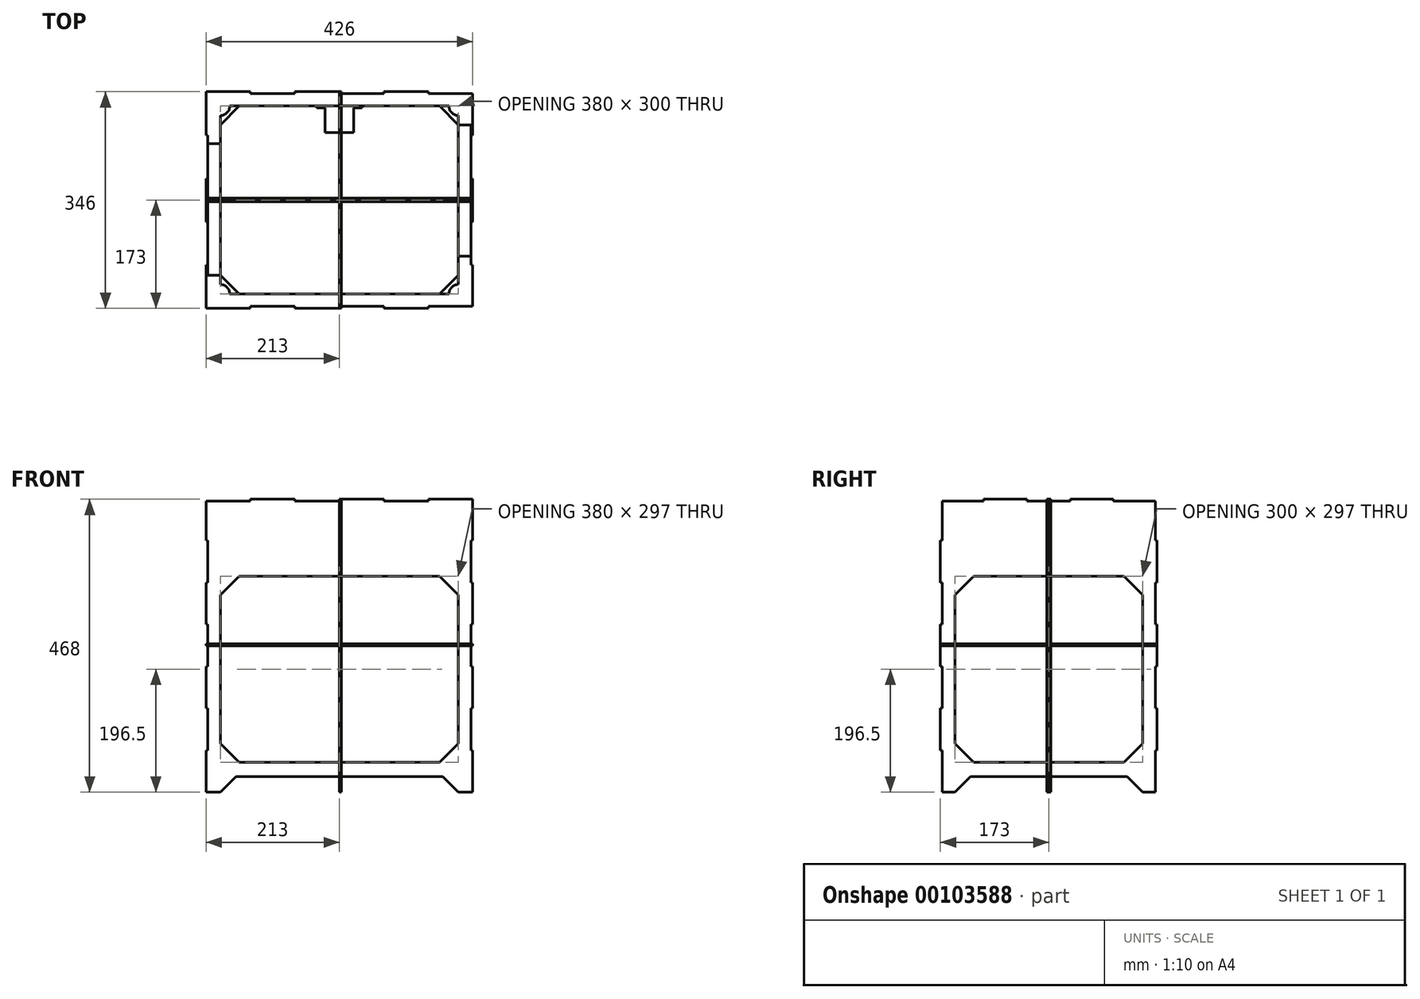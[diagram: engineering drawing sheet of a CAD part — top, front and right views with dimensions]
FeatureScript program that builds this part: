
annotation { "Feature Type Name" : "Feature", "Feature Type Description" : "" }
export const myFeature = defineFeature(function(context is Context, id is Id, definition is map)
    precondition{}
    {
        {
            assignVariable(context, id + "F0", {"name" : "thick", "anyValue" : 3});
        }
        {
            var Q0;
            Q0=qCreatedBy(makeId("Top.planeOp"),FACE);
            var sketch = newSketch(context, id + "F1", { "sketchPlane" : qUnion([Q0])});
            skLineSegment(sketch, "E0.bottom", {"start": v(213, -173) * mm, "end": v(-213, -173) * mm});
            skLineSegment(sketch, "E0.top", {"start": v(213, 173) * mm, "end": v(-213, 173) * mm});
            skLineSegment(sketch, "E0.left", {"start": v(213, -173) * mm, "end": v(213, 173) * mm});
            skLineSegment(sketch, "E0.right", {"start": v(-213, -173) * mm, "end": v(-213, 173) * mm});
            skPoint(sketch, "E0.middle", {"position": v(0, 0) * mm});
            skLineSegment(sketch, "E1.bottom", {"start": v(190, -150) * mm, "end": v(-190, -150) * mm, "construction": true});
            skLineSegment(sketch, "E1.top", {"start": v(190, 150) * mm, "end": v(-190, 150) * mm, "construction": true});
            skLineSegment(sketch, "E1.left", {"start": v(190, -150) * mm, "end": v(190, 150) * mm, "construction": true});
            skLineSegment(sketch, "E1.right", {"start": v(-190, -150) * mm, "end": v(-190, 150) * mm, "construction": true});
            skLineSegment(sketch, "E2", {"start": v(-160, 150) * mm, "end": v(-190, 120) * mm});
            skLineSegment(sketch, "E3", {"start": v(-190, 120) * mm, "end": v(-190, -120) * mm});
            skLineSegment(sketch, "E4", {"start": v(-190, -120) * mm, "end": v(-160, -150) * mm});
            skLineSegment(sketch, "E5", {"start": v(-160, -150) * mm, "end": v(160, -150) * mm});
            skLineSegment(sketch, "E6", {"start": v(160, -150) * mm, "end": v(190, -120) * mm});
            skLineSegment(sketch, "E7", {"start": v(190, -120) * mm, "end": v(190, 120) * mm});
            skLineSegment(sketch, "E8", {"start": v(190, 120) * mm, "end": v(160, 150) * mm});
            skLineSegment(sketch, "E9", {"start": v(160, 150) * mm, "end": v(-160, 150) * mm});
            skLineSegment(sketch, "E10.bottom", {"start": v(-142, 173) * mm, "end": v(-71, 173) * mm});
            skLineSegment(sketch, "E10.top", {"start": v(-142, 170) * mm, "end": v(-71, 170) * mm});
            skLineSegment(sketch, "E10.left", {"start": v(-142, 173) * mm, "end": v(-142, 170) * mm});
            skLineSegment(sketch, "E10.right", {"start": v(-71, 173) * mm, "end": v(-71, 170) * mm});
            skLineSegment(sketch, "E11.bottom", {"start": v(0, 173) * mm, "end": v(71, 173) * mm});
            skLineSegment(sketch, "E11.top", {"start": v(0, 170) * mm, "end": v(71, 170) * mm});
            skLineSegment(sketch, "E11.left", {"start": v(0, 173) * mm, "end": v(0, 170) * mm});
            skLineSegment(sketch, "E11.right", {"start": v(71, 173) * mm, "end": v(71, 170) * mm});
            skLineSegment(sketch, "E12.bottom", {"start": v(142, 173) * mm, "end": v(213, 173) * mm});
            skLineSegment(sketch, "E12.top", {"start": v(142, 170) * mm, "end": v(213, 170) * mm});
            skLineSegment(sketch, "E12.left", {"start": v(142, 173) * mm, "end": v(142, 170) * mm});
            skLineSegment(sketch, "E12.right", {"start": v(213, 173) * mm, "end": v(213, 170) * mm});
            skLineSegment(sketch, "E13.bottom", {"start": v(-142, -173) * mm, "end": v(-71, -173) * mm});
            skLineSegment(sketch, "E13.top", {"start": v(-142, -170) * mm, "end": v(-71, -170) * mm});
            skLineSegment(sketch, "E13.left", {"start": v(-142, -173) * mm, "end": v(-142, -170) * mm});
            skLineSegment(sketch, "E13.right", {"start": v(-71, -173) * mm, "end": v(-71, -170) * mm});
            skLineSegment(sketch, "E14.bottom", {"start": v(0, -173) * mm, "end": v(71, -173) * mm});
            skLineSegment(sketch, "E14.top", {"start": v(0, -170) * mm, "end": v(71, -170) * mm});
            skLineSegment(sketch, "E14.left", {"start": v(0, -173) * mm, "end": v(0, -170) * mm});
            skLineSegment(sketch, "E14.right", {"start": v(71, -173) * mm, "end": v(71, -170) * mm});
            skLineSegment(sketch, "E15.bottom", {"start": v(142, -173) * mm, "end": v(213, -173) * mm});
            skLineSegment(sketch, "E15.top", {"start": v(142, -170) * mm, "end": v(213, -170) * mm});
            skLineSegment(sketch, "E15.left", {"start": v(142, -173) * mm, "end": v(142, -170) * mm});
            skLineSegment(sketch, "E15.right", {"start": v(213, -173) * mm, "end": v(213, -170) * mm});
            skLineSegment(sketch, "E16.bottom", {"start": v(-213, 103) * mm, "end": v(-210, 103) * mm});
            skLineSegment(sketch, "E16.top", {"start": v(-213, 34) * mm, "end": v(-210, 34) * mm});
            skLineSegment(sketch, "E16.left", {"start": v(-213, 103) * mm, "end": v(-213, 34) * mm});
            skLineSegment(sketch, "E16.right", {"start": v(-210, 103) * mm, "end": v(-210, 34) * mm});
            skLineSegment(sketch, "E17.0.1.0", {"start": v(-213, -35) * mm, "end": v(-210, -35) * mm});
            skLineSegment(sketch, "E17.0.1.1", {"start": v(-210, -35) * mm, "end": v(-210, -104) * mm});
            skLineSegment(sketch, "E17.0.1.2", {"start": v(-213, -104) * mm, "end": v(-210, -104) * mm});
            skLineSegment(sketch, "E17.direction1", {"start": v(-213, 103) * mm, "end": v(-210, 103) * mm, "construction": true});
            skLineSegment(sketch, "E17.direction2", {"start": v(-213, 103) * mm, "end": v(-213, -35) * mm, "construction": true});
            skLineSegment(sketch, "E18.bottom", {"start": v(213, 103) * mm, "end": v(210, 103) * mm});
            skLineSegment(sketch, "E18.top", {"start": v(213, 34) * mm, "end": v(210, 34) * mm});
            skLineSegment(sketch, "E18.left", {"start": v(213, 103) * mm, "end": v(213, 34) * mm});
            skLineSegment(sketch, "E18.right", {"start": v(210, 103) * mm, "end": v(210, 34) * mm});
            skLineSegment(sketch, "E19.bottom", {"start": v(213, -35) * mm, "end": v(210, -35) * mm});
            skLineSegment(sketch, "E19.top", {"start": v(213, -104) * mm, "end": v(210, -104) * mm});
            skLineSegment(sketch, "E19.left", {"start": v(213, -35) * mm, "end": v(213, -104) * mm});
            skLineSegment(sketch, "E19.right", {"start": v(210, -35) * mm, "end": v(210, -104) * mm});
            skSolve(sketch);
        }
        {
            var Q0;
            Q0=makeQuery(id+"F1.imprint","IMPRINT",FACE,{"disambiguationData":[TD([[makeQuery(id+"F1.imprint","IMPRINT",EDGE,{"derivedFrom":sQuery(id+"F1.wireOp",EDGE,"E0.left")}),1.0]])]});
            extrude(context, id + "F2", {"entities" : qUnion([Q0]), "depth" : (getVariable(context, 'thick')) * mm});
        }
        {
            var Q0;
            Q0=qCreatedBy(makeId("Front.planeOp"),FACE);
            var sketch = newSketch(context, id + "F3", { "sketchPlane" : qUnion([Q0])});
            skLineSegment(sketch, "E20.bottom", {"start": v(213, -234) * mm, "end": v(-213, -234) * mm});
            skLineSegment(sketch, "E20.top", {"start": v(213, 234) * mm, "end": v(-213, 234) * mm});
            skLineSegment(sketch, "E20.left", {"start": v(213, -234) * mm, "end": v(213, 234) * mm});
            skLineSegment(sketch, "E20.right", {"start": v(-213, -234) * mm, "end": v(-213, 234) * mm});
            skPoint(sketch, "E20.middle", {"position": v(0, 0) * mm});
            skLineSegment(sketch, "E21.bottom", {"start": v(-190, 111) * mm, "end": v(190, 111) * mm, "construction": true});
            skLineSegment(sketch, "E21.top", {"start": v(-190, -186) * mm, "end": v(190, -186) * mm, "construction": true});
            skLineSegment(sketch, "E21.left", {"start": v(-190, 111) * mm, "end": v(-190, -186) * mm, "construction": true});
            skLineSegment(sketch, "E21.right", {"start": v(190, 111) * mm, "end": v(190, -186) * mm, "construction": true});
            skLineSegment(sketch, "E22", {"start": v(-190, -234) * mm, "end": v(-165, -209) * mm});
            skLineSegment(sketch, "E23", {"start": v(-165, -209) * mm, "end": v(165, -209) * mm});
            skLineSegment(sketch, "E24", {"start": v(165, -209) * mm, "end": v(190, -234) * mm});
            skLineSegment(sketch, "E25", {"start": v(-160, 111) * mm, "end": v(-190, 81) * mm});
            skLineSegment(sketch, "E26", {"start": v(-190, 81) * mm, "end": v(-190, -156) * mm});
            skLineSegment(sketch, "E27", {"start": v(-190, -156) * mm, "end": v(-160, -186) * mm});
            skLineSegment(sketch, "E28", {"start": v(-160, -186) * mm, "end": v(160, -186) * mm});
            skLineSegment(sketch, "E29", {"start": v(160, -186) * mm, "end": v(190, -156) * mm});
            skLineSegment(sketch, "E30", {"start": v(190, -156) * mm, "end": v(190, 81) * mm});
            skLineSegment(sketch, "E31", {"start": v(190, 81) * mm, "end": v(160, 111) * mm});
            skLineSegment(sketch, "E32", {"start": v(160, 111) * mm, "end": v(-160, 111) * mm});
            skLineSegment(sketch, "E33.bottom", {"start": v(-213, 234) * mm, "end": v(-142, 234) * mm});
            skLineSegment(sketch, "E33.top", {"start": v(-213, 231) * mm, "end": v(-142, 231) * mm});
            skLineSegment(sketch, "E33.left", {"start": v(-213, 234) * mm, "end": v(-213, 231) * mm});
            skLineSegment(sketch, "E33.right", {"start": v(-142, 234) * mm, "end": v(-142, 231) * mm});
            skLineSegment(sketch, "E34.1.0.0", {"start": v(-71, 231) * mm, "end": v(0, 231) * mm});
            skLineSegment(sketch, "E34.1.0.1", {"start": v(-71, 234) * mm, "end": v(-71, 231) * mm});
            skLineSegment(sketch, "E34.1.0.2", {"start": v(0, 234) * mm, "end": v(0, 231) * mm});
            skLineSegment(sketch, "E34.2.0.0", {"start": v(71, 231) * mm, "end": v(142, 231) * mm});
            skLineSegment(sketch, "E34.2.0.1", {"start": v(71, 234) * mm, "end": v(71, 231) * mm});
            skLineSegment(sketch, "E34.2.0.2", {"start": v(142, 234) * mm, "end": v(142, 231) * mm});
            skLineSegment(sketch, "E34.direction1", {"start": v(-213, 231) * mm, "end": v(-71, 231) * mm, "construction": true});
            skLineSegment(sketch, "E35.bottom", {"start": v(-213, 168) * mm, "end": v(-210, 168) * mm});
            skLineSegment(sketch, "E35.top", {"start": v(-213, 101) * mm, "end": v(-210, 101) * mm});
            skLineSegment(sketch, "E35.left", {"start": v(-213, 168) * mm, "end": v(-213, 101) * mm});
            skLineSegment(sketch, "E35.right", {"start": v(-210, 168) * mm, "end": v(-210, 101) * mm});
            skLineSegment(sketch, "E36.0.1.0", {"start": v(-210, 34) * mm, "end": v(-210, -33) * mm});
            skLineSegment(sketch, "E36.0.1.1", {"start": v(-213, 34) * mm, "end": v(-210, 34) * mm});
            skLineSegment(sketch, "E36.0.1.2", {"start": v(-213, -33) * mm, "end": v(-210, -33) * mm});
            skLineSegment(sketch, "E36.0.2.0", {"start": v(-210, -100) * mm, "end": v(-210, -167) * mm});
            skLineSegment(sketch, "E36.0.2.1", {"start": v(-213, -100) * mm, "end": v(-210, -100) * mm});
            skLineSegment(sketch, "E36.0.2.2", {"start": v(-213, -167) * mm, "end": v(-210, -167) * mm});
            skLineSegment(sketch, "E36.direction1", {"start": v(-210, 101) * mm, "end": v(-210, 101) * mm});
            skLineSegment(sketch, "E36.direction2", {"start": v(-210, 101) * mm, "end": v(-210, -33) * mm, "construction": true});
            skLineSegment(sketch, "E37.bottom", {"start": v(213, 168) * mm, "end": v(210, 168) * mm});
            skLineSegment(sketch, "E37.top", {"start": v(213, 101) * mm, "end": v(210, 101) * mm});
            skLineSegment(sketch, "E37.left", {"start": v(213, 168) * mm, "end": v(213, 101) * mm});
            skLineSegment(sketch, "E37.right", {"start": v(210, 168) * mm, "end": v(210, 101) * mm});
            skLineSegment(sketch, "E38.0.1.0", {"start": v(213, 34) * mm, "end": v(210, 34) * mm});
            skLineSegment(sketch, "E38.0.1.1", {"start": v(210, 34) * mm, "end": v(210, -33) * mm});
            skLineSegment(sketch, "E38.0.1.2", {"start": v(213, -33) * mm, "end": v(210, -33) * mm});
            skLineSegment(sketch, "E38.0.2.0", {"start": v(213, -100) * mm, "end": v(210, -100) * mm});
            skLineSegment(sketch, "E38.0.2.1", {"start": v(210, -100) * mm, "end": v(210, -167) * mm});
            skLineSegment(sketch, "E38.0.2.2", {"start": v(213, -167) * mm, "end": v(210, -167) * mm});
            skLineSegment(sketch, "E38.direction1", {"start": v(210, 168) * mm, "end": v(213, 168) * mm, "construction": true});
            skLineSegment(sketch, "E38.direction2", {"start": v(210, 168) * mm, "end": v(210, 34) * mm, "construction": true});
            skSolve(sketch);
        }
        {
            var Q0;
            {var subQ10=sQuery(id+"F3.wireOp",EDGE,"E20.left");Q0=makeQuery(id+"F3.imprint","IMPRINT",FACE,{"disambiguationData":[TD([[makeQuery(id+"F3.imprint","IMPRINT",EDGE,{"derivedFrom":subQ10}),1.0]])]});}
            extrude(context, id + "F4", {"entities" : qUnion([Q0]), "depth" : (getVariable(context, 'thick')) * mm});
        }
        {
            var Q0;
            Q0=makeQuery(id+"F4.opExtrude","CAP_FACE",FACE,{"disambiguationData":[OSD([sQuery(id+"F3.wireOp",EDGE,"E20.bottom"),sQuery(id+"F3.wireOp",EDGE,"E20.top"),sQuery(id+"F3.wireOp",EDGE,"E20.left"),sQuery(id+"F3.wireOp",EDGE,"E20.right"),sQuery(id+"F3.wireOp",EDGE,"E22"),sQuery(id+"F3.wireOp",EDGE,"E23"),sQuery(id+"F3.wireOp",EDGE,"E24"),sQuery(id+"F3.wireOp",EDGE,"E25"),sQuery(id+"F3.wireOp",EDGE,"E26"),sQuery(id+"F3.wireOp",EDGE,"E27"),sQuery(id+"F3.wireOp",EDGE,"E28"),sQuery(id+"F3.wireOp",EDGE,"E29"),sQuery(id+"F3.wireOp",EDGE,"E30"),sQuery(id+"F3.wireOp",EDGE,"E31"),sQuery(id+"F3.wireOp",EDGE,"E32"),sQuery(id+"F3.wireOp",EDGE,"E33.top"),sQuery(id+"F3.wireOp",EDGE,"E33.right"),sQuery(id+"F3.wireOp",EDGE,"E34.1.0.0"),sQuery(id+"F3.wireOp",EDGE,"E34.1.0.1"),sQuery(id+"F3.wireOp",EDGE,"E34.1.0.2"),sQuery(id+"F3.wireOp",EDGE,"E34.2.0.0"),sQuery(id+"F3.wireOp",EDGE,"E34.2.0.1"),sQuery(id+"F3.wireOp",EDGE,"E34.2.0.2"),sQuery(id+"F3.wireOp",EDGE,"E35.bottom"),sQuery(id+"F3.wireOp",EDGE,"E35.top"),sQuery(id+"F3.wireOp",EDGE,"E35.right"),sQuery(id+"F3.wireOp",EDGE,"E36.0.1.0"),sQuery(id+"F3.wireOp",EDGE,"E36.0.1.1"),sQuery(id+"F3.wireOp",EDGE,"E36.0.1.2"),sQuery(id+"F3.wireOp",EDGE,"E36.0.2.0"),sQuery(id+"F3.wireOp",EDGE,"E36.0.2.1"),sQuery(id+"F3.wireOp",EDGE,"E36.0.2.2"),sQuery(id+"F3.wireOp",EDGE,"E37.bottom"),sQuery(id+"F3.wireOp",EDGE,"E37.top"),sQuery(id+"F3.wireOp",EDGE,"E37.right"),sQuery(id+"F3.wireOp",EDGE,"E38.0.1.0"),sQuery(id+"F3.wireOp",EDGE,"E38.0.1.1"),sQuery(id+"F3.wireOp",EDGE,"E38.0.1.2"),sQuery(id+"F3.wireOp",EDGE,"E38.0.2.0"),sQuery(id+"F3.wireOp",EDGE,"E38.0.2.1"),sQuery(id+"F3.wireOp",EDGE,"E38.0.2.2")])],"isStart":false});
            var sketch = newSketch(context, id + "F5", { "sketchPlane" : qUnion([Q0])});
            skLineSegment(sketch, "E39.bottom", {"start": v(-19.3, 136) * mm, "end": v(150, 136) * mm, "construction": true});
            skLineSegment(sketch, "E39.top", {"start": v(-19.3, 205.7) * mm, "end": v(150, 205.7) * mm, "construction": true});
            skLineSegment(sketch, "E39.left", {"start": v(-19.3, 136) * mm, "end": v(-19.3, 205.7) * mm, "construction": true});
            skLineSegment(sketch, "E39.right", {"start": v(150, 136) * mm, "end": v(150, 205.7) * mm, "construction": true});
            skCircle(sketch, "E40", {"center": v(-7.15, 195.6) * mm, "radius": 1.8 * mm});
            skCircle(sketch, "E41", {"center": v(-7.15, 145.6) * mm, "radius": 1.8 * mm});
            skCircle(sketch, "E42", {"center": v(137.85, 195.6) * mm, "radius": 1.8 * mm});
            skCircle(sketch, "E43", {"center": v(137.85, 145.6) * mm, "radius": 1.8 * mm});
            skCircle(sketch, "E44", {"center": v(127.7, 168.1) * mm, "radius": 5 * mm});
            skCircle(sketch, "E45", {"center": v(126.85, 187.6) * mm, "radius": 7.5 * mm});
            skCircle(sketch, "E46", {"center": v(127.7, 149.6) * mm, "radius": 4.32 * mm});
            skLineSegment(sketch, "E47.bottom", {"start": v(3, 184.8) * mm, "end": v(101.4, 184.8) * mm});
            skLineSegment(sketch, "E47.top", {"start": v(3, 144.4) * mm, "end": v(101.4, 144.4) * mm});
            skLineSegment(sketch, "E47.left", {"start": v(3, 184.8) * mm, "end": v(3, 144.4) * mm});
            skLineSegment(sketch, "E47.right", {"start": v(101.4, 184.8) * mm, "end": v(101.4, 144.4) * mm});
            skSolve(sketch);
        }
        {
            var Q0;
            {var subQ10=sQuery(id+"F3.wireOp",EDGE,"E20.left");Q0=makeQuery(id+"F3.imprint","IMPRINT",FACE,{"disambiguationData":[TD([[makeQuery(id+"F3.imprint","IMPRINT",EDGE,{"derivedFrom":subQ10}),1.0]])]});}
            var Q1;
            Q1=makeQuery(id+"F3.imprint","IMPRINT",FACE,{"disambiguationData":[TD([[makeQuery(id+"F3.imprint","IMPRINT",EDGE,{"derivedFrom":sQuery(id+"F3.wireOp",EDGE,"E25")}),1.0]])]});
            extrude(context, id + "F6", {"entities" : qUnion([Q0, Q1]), "oppositeDirection" : true, "depth" : (getVariable(context, 'thick')) * mm});
        }
        {
            var Q0;
            Q0=qCreatedBy(makeId("Right.planeOp"),FACE);
            var sketch = newSketch(context, id + "F7", { "sketchPlane" : qUnion([Q0])});
            skLineSegment(sketch, "E48.bottom", {"start": v(-173, 234) * mm, "end": v(173, 234) * mm});
            skLineSegment(sketch, "E48.top", {"start": v(-173, -234) * mm, "end": v(173, -234) * mm});
            skLineSegment(sketch, "E48.left", {"start": v(-173, 234) * mm, "end": v(-173, -234) * mm});
            skLineSegment(sketch, "E48.right", {"start": v(173, 234) * mm, "end": v(173, -234) * mm});
            skPoint(sketch, "E48.middle", {"position": v(0, 0) * mm});
            skLineSegment(sketch, "E49.bottom", {"start": v(150, 111) * mm, "end": v(-150, 111) * mm, "construction": true});
            skLineSegment(sketch, "E49.top", {"start": v(150, -186) * mm, "end": v(-150, -186) * mm, "construction": true});
            skLineSegment(sketch, "E49.left", {"start": v(150, 111) * mm, "end": v(150, -186) * mm, "construction": true});
            skLineSegment(sketch, "E49.right", {"start": v(-150, 111) * mm, "end": v(-150, -186) * mm, "construction": true});
            skLineSegment(sketch, "E50", {"start": v(150, -234) * mm, "end": v(125, -209) * mm});
            skLineSegment(sketch, "E51", {"start": v(125, -209) * mm, "end": v(-125, -209) * mm});
            skLineSegment(sketch, "E52", {"start": v(-125, -209) * mm, "end": v(-150, -234) * mm});
            skLineSegment(sketch, "E53.bottom", {"start": v(172, 234) * mm, "end": v(103, 234) * mm});
            skLineSegment(sketch, "E53.top", {"start": v(172, 231) * mm, "end": v(103, 231) * mm});
            skLineSegment(sketch, "E53.left", {"start": v(172, 234) * mm, "end": v(172, 231) * mm});
            skLineSegment(sketch, "E53.right", {"start": v(103, 234) * mm, "end": v(103, 231) * mm});
            skLineSegment(sketch, "E54.1.0.0", {"start": v(34, 234) * mm, "end": v(34, 231) * mm});
            skLineSegment(sketch, "E54.1.0.1", {"start": v(34, 231) * mm, "end": v(-35, 231) * mm});
            skLineSegment(sketch, "E54.1.0.2", {"start": v(-35, 234) * mm, "end": v(-35, 231) * mm});
            skLineSegment(sketch, "E54.2.0.0", {"start": v(-104, 234) * mm, "end": v(-104, 231) * mm});
            skLineSegment(sketch, "E54.2.0.1", {"start": v(-104, 231) * mm, "end": v(-173, 231) * mm});
            skLineSegment(sketch, "E54.2.0.2", {"start": v(-173, 234) * mm, "end": v(-173, 231) * mm});
            skLineSegment(sketch, "E54.direction1", {"start": v(172, 231) * mm, "end": v(34, 231) * mm, "construction": true});
            skLineSegment(sketch, "E55", {"start": v(120, 111) * mm, "end": v(150, 81) * mm});
            skLineSegment(sketch, "E56", {"start": v(150, 81) * mm, "end": v(150, -156) * mm});
            skLineSegment(sketch, "E57", {"start": v(150, -156) * mm, "end": v(120, -186) * mm});
            skLineSegment(sketch, "E58", {"start": v(120, -186) * mm, "end": v(-120, -186) * mm});
            skLineSegment(sketch, "E59", {"start": v(-120, -186) * mm, "end": v(-150, -156) * mm});
            skLineSegment(sketch, "E60", {"start": v(-150, -156) * mm, "end": v(-150, 81) * mm});
            skLineSegment(sketch, "E61", {"start": v(-150, 81) * mm, "end": v(-120, 111) * mm});
            skLineSegment(sketch, "E62", {"start": v(-120, 111) * mm, "end": v(120, 111) * mm});
            skLineSegment(sketch, "E63.bottom", {"start": v(-173, 235) * mm, "end": v(-170, 235) * mm});
            skLineSegment(sketch, "E63.top", {"start": v(-173, 168) * mm, "end": v(-170, 168) * mm});
            skLineSegment(sketch, "E63.left", {"start": v(-173, 235) * mm, "end": v(-173, 168) * mm});
            skLineSegment(sketch, "E63.right", {"start": v(-170, 235) * mm, "end": v(-170, 168) * mm});
            skLineSegment(sketch, "E64.0.1.0", {"start": v(-173, 34) * mm, "end": v(-170, 34) * mm});
            skLineSegment(sketch, "E64.0.1.1", {"start": v(-170, 101) * mm, "end": v(-170, 34) * mm});
            skLineSegment(sketch, "E64.0.1.2", {"start": v(-173, 101) * mm, "end": v(-170, 101) * mm});
            skLineSegment(sketch, "E64.0.2.0", {"start": v(-173, -100) * mm, "end": v(-170, -100) * mm});
            skLineSegment(sketch, "E64.0.2.1", {"start": v(-170, -33) * mm, "end": v(-170, -100) * mm});
            skLineSegment(sketch, "E64.0.2.2", {"start": v(-173, -33) * mm, "end": v(-170, -33) * mm});
            skLineSegment(sketch, "E64.0.3.0", {"start": v(-173, -234) * mm, "end": v(-170, -234) * mm});
            skLineSegment(sketch, "E64.0.3.1", {"start": v(-170, -167) * mm, "end": v(-170, -234) * mm});
            skLineSegment(sketch, "E64.0.3.2", {"start": v(-173, -167) * mm, "end": v(-170, -167) * mm});
            skLineSegment(sketch, "E64.direction1", {"start": v(-173, 168) * mm, "end": v(-170, 168) * mm, "construction": true});
            skLineSegment(sketch, "E64.direction2", {"start": v(-173, 168) * mm, "end": v(-173, 34) * mm, "construction": true});
            skLineSegment(sketch, "E65.bottom", {"start": v(173, 235) * mm, "end": v(170, 235) * mm});
            skLineSegment(sketch, "E65.top", {"start": v(173, 168) * mm, "end": v(170, 168) * mm});
            skLineSegment(sketch, "E65.left", {"start": v(173, 235) * mm, "end": v(173, 168) * mm});
            skLineSegment(sketch, "E65.right", {"start": v(170, 235) * mm, "end": v(170, 168) * mm});
            skLineSegment(sketch, "E66.0.1.0", {"start": v(173, 101) * mm, "end": v(170, 101) * mm});
            skLineSegment(sketch, "E66.0.1.1", {"start": v(170, 101) * mm, "end": v(170, 34) * mm});
            skLineSegment(sketch, "E66.0.1.2", {"start": v(173, 34) * mm, "end": v(170, 34) * mm});
            skLineSegment(sketch, "E66.0.2.0", {"start": v(173, -33) * mm, "end": v(170, -33) * mm});
            skLineSegment(sketch, "E66.0.2.1", {"start": v(170, -33) * mm, "end": v(170, -100) * mm});
            skLineSegment(sketch, "E66.0.2.2", {"start": v(173, -100) * mm, "end": v(170, -100) * mm});
            skLineSegment(sketch, "E66.0.3.0", {"start": v(173, -167) * mm, "end": v(170, -167) * mm});
            skLineSegment(sketch, "E66.0.3.1", {"start": v(170, -167) * mm, "end": v(170, -234) * mm});
            skLineSegment(sketch, "E66.0.3.2", {"start": v(173, -234) * mm, "end": v(170, -234) * mm});
            skLineSegment(sketch, "E66.direction1", {"start": v(170, 235) * mm, "end": v(170, 235) * mm});
            skLineSegment(sketch, "E66.direction2", {"start": v(170, 235) * mm, "end": v(170, 101) * mm, "construction": true});
            skSolve(sketch);
        }
        {
            var Q0;
            {var subQ3=sQuery(id+"F7.wireOp",EDGE,"E48.left");Q0=makeQuery(id+"F7.imprint","IMPRINT",FACE,{"disambiguationData":[TD([[makeQuery(id+"F7.imprint","IMPRINT",EDGE,{"derivedFrom":subQ3}),1.0]])]});}
            extrude(context, id + "F8", {"entities" : qUnion([Q0]), "depth" : (getVariable(context, 'thick')) * mm});
        }
        {
            var Q0;
            Q0=qCreatedBy(makeId("Top.planeOp"),FACE);
            var sketch = newSketch(context, id + "F9", { "sketchPlane" : qUnion([Q0])});
            skLineSegment(sketch, "E67.bottom", {"start": v(190, -150) * mm, "end": v(-190, -150) * mm});
            skLineSegment(sketch, "E67.top", {"start": v(190, 150) * mm, "end": v(-190, 150) * mm});
            skLineSegment(sketch, "E67.left", {"start": v(190, -150) * mm, "end": v(190, 150) * mm});
            skLineSegment(sketch, "E67.right", {"start": v(-190, -150) * mm, "end": v(-190, 150) * mm});
            skPoint(sketch, "E67.middle", {"position": v(0, 0) * mm});
            skLineSegment(sketch, "E68.bottom", {"start": v(-23.15, 150) * mm, "end": v(23.15, 150) * mm});
            skLineSegment(sketch, "E68.top", {"start": v(-23.15, 107.7) * mm, "end": v(23.15, 107.7) * mm});
            skLineSegment(sketch, "E68.left", {"start": v(-23.15, 150) * mm, "end": v(-23.15, 107.7) * mm});
            skLineSegment(sketch, "E68.right", {"start": v(23.15, 150) * mm, "end": v(23.15, 107.7) * mm});
            skLineSegment(sketch, "E69", {"start": v(0, 0) * mm, "end": v(0, 107.7) * mm, "construction": true});
            skLineSegment(sketch, "E70", {"start": v(-23.15, 147) * mm, "end": v(-36.15, 147) * mm});
            skLineSegment(sketch, "E71", {"start": v(-36.15, 147) * mm, "end": v(-36.15, 150) * mm});
            skLineSegment(sketch, "E72", {"start": v(23.15, 147) * mm, "end": v(36.15, 147) * mm});
            skLineSegment(sketch, "E73", {"start": v(36.15, 147) * mm, "end": v(36.15, 150) * mm});
            skLineSegment(sketch, "E74.bottom", {"start": v(-190, 90) * mm, "end": v(-210, 90) * mm});
            skLineSegment(sketch, "E74.top", {"start": v(-190, -120) * mm, "end": v(-210, -120) * mm});
            skLineSegment(sketch, "E74.left", {"start": v(-190, 90) * mm, "end": v(-190, -120) * mm});
            skLineSegment(sketch, "E74.right", {"start": v(-210, 90) * mm, "end": v(-210, -120) * mm});
            skLineSegment(sketch, "E75.bottom", {"start": v(190, 120) * mm, "end": v(210, 120) * mm});
            skLineSegment(sketch, "E75.top", {"start": v(190, -90) * mm, "end": v(210, -90) * mm});
            skLineSegment(sketch, "E75.left", {"start": v(190, 120) * mm, "end": v(190, -90) * mm});
            skLineSegment(sketch, "E75.right", {"start": v(210, 120) * mm, "end": v(210, -90) * mm});
            skLineSegment(sketch, "E76.bottom", {"start": v(-160, -150) * mm, "end": v(160, -150) * mm});
            skLineSegment(sketch, "E76.top", {"start": v(-160, -170) * mm, "end": v(160, -170) * mm});
            skLineSegment(sketch, "E76.left", {"start": v(-160, -150) * mm, "end": v(-160, -170) * mm});
            skLineSegment(sketch, "E76.right", {"start": v(160, -150) * mm, "end": v(160, -170) * mm});
            skArc(sketch, "E77", {"start": v(-190, -135) * mm, "mid": v(-179.4, -139.4) * mm, "end": v(-175, -150) * mm});
            skArc(sketch, "E78", {"start": v(190, -135) * mm, "mid": v(179.4, -139.4) * mm, "end": v(175, -150) * mm});
            skArc(sketch, "E79", {"start": v(-190, 135) * mm, "mid": v(-179.4, 139.4) * mm, "end": v(-175, 150) * mm});
            skArc(sketch, "E80", {"start": v(175, 150) * mm, "mid": v(179.4, 139.4) * mm, "end": v(190, 135) * mm});
            skSolve(sketch);
        }
        {
            var Q0;
            {var subQ8=sQuery(id+"F9.wireOp",EDGE,"E67.bottom");Q0=makeQuery(id+"F9.imprint","IMPRINT",FACE,{"disambiguationData":[TD([[makeQuery(id+"F9.imprint","IMPRINT",EDGE,{"derivedFrom":subQ8}),-1.0]])]});}
            var Q1;
            Q1=makeQuery(id+"F9.imprint","IMPRINT",FACE,{"disambiguationData":[TD([[makeQuery(id+"F9.imprint","IMPRINT",EDGE,{"derivedFrom":sQuery(id+"F9.wireOp",EDGE,"E74.bottom")}),1.0]])]});
            var Q2;
            Q2=makeQuery(id+"F9.imprint","IMPRINT",FACE,{"disambiguationData":[TD([[makeQuery(id+"F9.imprint","IMPRINT",EDGE,{"derivedFrom":sQuery(id+"F9.wireOp",EDGE,"E75.bottom")}),-1.0]])]});
            var Q3;
            Q3=makeQuery(id+"F9.imprint","IMPRINT",FACE,{"disambiguationData":[TD([[makeQuery(id+"F9.imprint","IMPRINT",EDGE,{"derivedFrom":sQuery(id+"F9.wireOp",EDGE,"E76.bottom")}),-1.0]])]});
            extrude(context, id + "F10", {"entities" : qUnion([Q0, Q1, Q2, Q3]), "depth" : (getVariable(context, 'thick')) * mm});
        }
    });
